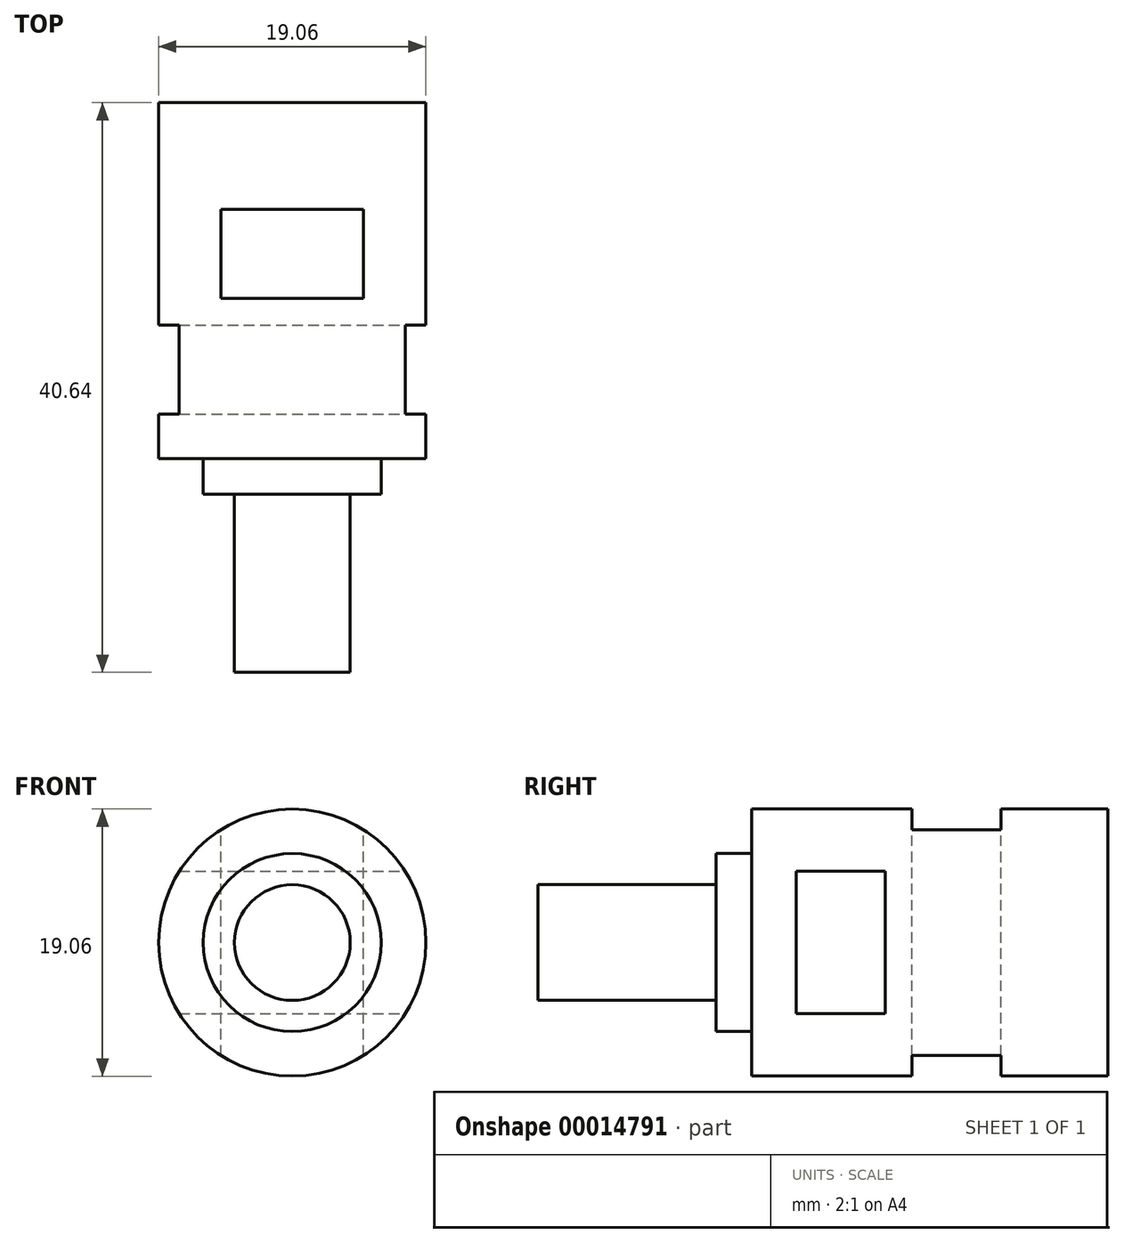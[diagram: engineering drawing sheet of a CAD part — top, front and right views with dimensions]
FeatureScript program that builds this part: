
annotation { "Feature Type Name" : "Feature", "Feature Type Description" : "" }
export const myFeature = defineFeature(function(context is Context, id is Id, definition is map)
    precondition{}
    {
        {
            var Q0;
            Q0=qCreatedBy(makeId("Front.planeOp"),FACE);
            var sketch = newSketch(context, id + "F0", { "sketchPlane" : qUnion([Q0])});
            skCircle(sketch, "E0", {"center": v(0, 0) * mm, "radius": 9.53 * mm});
            skSolve(sketch);
        }
        {
            var Q0;
            Q0=makeQuery(id+"F0.imprint","IMPRINT",FACE,{"disambiguationData":[TD([[makeQuery(id+"F0.imprint","IMPRINT",EDGE,{"derivedFrom":sQuery(id+"F0.wireOp",EDGE,"E0")}),1.0]])]});
            extrude(context, id + "F1", {"entities" : qUnion([Q0]), "depth" : 25.4 * mm});
        }
        {
            var Q0;
            Q0=makeQuery(id+"F1.opExtrude","CAP_FACE",FACE,{"disambiguationData":[OSD([sQuery(id+"F0.wireOp",EDGE,"E0")])],"isStart":false});
            var sketch = newSketch(context, id + "F2", { "sketchPlane" : qUnion([Q0])});
            skCircle(sketch, "E1", {"center": v(0, 0) * mm, "radius": 6.35 * mm});
            skSolve(sketch);
        }
        {
            var Q0;
            Q0=makeQuery(id+"F2.imprint","IMPRINT",FACE,{"disambiguationData":[TD([[makeQuery(id+"F2.imprint","IMPRINT",EDGE,{"derivedFrom":sQuery(id+"F2.wireOp",EDGE,"E1")}),1.0]])]});
            extrude(context, id + "F3", {"entities" : qUnion([Q0]), "operationType" : NewBodyOperationType.ADD, "depth" : 2.54 * mm});
        }
        {
            var Q0;
            Q0=makeQuery(id+"F3.opExtrude","CAP_FACE",FACE,{"disambiguationData":[OSD([sQuery(id+"F2.wireOp",EDGE,"E1")])],"isStart":false});
            var sketch = newSketch(context, id + "F4", { "sketchPlane" : qUnion([Q0])});
            skCircle(sketch, "E2", {"center": v(0, 0) * mm, "radius": 4.13 * mm});
            skSolve(sketch);
        }
        {
            var Q0;
            Q0=makeQuery(id+"F4.imprint","IMPRINT",FACE,{"disambiguationData":[TD([[makeQuery(id+"F4.imprint","IMPRINT",EDGE,{"derivedFrom":sQuery(id+"F4.wireOp",EDGE,"E2")}),1.0]])]});
            extrude(context, id + "F5", {"entities" : qUnion([Q0]), "operationType" : NewBodyOperationType.ADD, "depth" : 12.7 * mm});
        }
        {
            var Q0;
            Q0=qCreatedBy(makeId("Top.planeOp"),FACE);
            var sketch = newSketch(context, id + "F6", { "sketchPlane" : qUnion([Q0])});
            skLineSegment(sketch, "E3.rect.bottom", {"start": v(5.08, -13.97) * mm, "end": v(-5.08, -13.97) * mm});
            skLineSegment(sketch, "E3.rect.top", {"start": v(5.08, -7.62) * mm, "end": v(-5.08, -7.62) * mm});
            skLineSegment(sketch, "E3.rect.left", {"start": v(5.08, -13.97) * mm, "end": v(5.08, -7.62) * mm});
            skLineSegment(sketch, "E3.rect.right", {"start": v(-5.08, -13.97) * mm, "end": v(-5.08, -7.62) * mm});
            skPoint(sketch, "E3.rect.middle", {"position": v(0, -10.8) * mm});
            skSolve(sketch);
        }
        {
            var Q0;
            Q0=qCreatedBy(makeId("Right.planeOp"),FACE);
            var sketch = newSketch(context, id + "F7", { "sketchPlane" : qUnion([Q0])});
            skLineSegment(sketch, "E4.rect.bottom", {"start": v(-15.88, -5.08) * mm, "end": v(-22.23, -5.08) * mm});
            skLineSegment(sketch, "E4.rect.top", {"start": v(-15.88, 5.08) * mm, "end": v(-22.22, 5.08) * mm});
            skLineSegment(sketch, "E4.rect.left", {"start": v(-15.88, -5.08) * mm, "end": v(-15.87, 5.08) * mm});
            skLineSegment(sketch, "E4.rect.right", {"start": v(-22.23, -5.08) * mm, "end": v(-22.22, 5.08) * mm});
            skPoint(sketch, "E4.rect.middle", {"position": v(-19.05, 0) * mm});
            skSolve(sketch);
        }
        {
            var Q0;
            Q0=qSketchRegion(id+"F7",true);
            extrude(context, id + "F8", {"entities" : qUnion([Q0]), "operationType" : NewBodyOperationType.REMOVE, "oppositeDirection" : true, "depth" : 25.4 * mm, "hasSecondDirection" : true, "secondDirectionOppositeDirection" : false, "secondDirectionDepth" : 25.4 * mm});
        }
        {
            var Q0;
            Q0=qSketchRegion(id+"F6",true);
            extrude(context, id + "F9", {"entities" : qUnion([Q0]), "operationType" : NewBodyOperationType.REMOVE, "oppositeDirection" : true, "depth" : 12.7 * mm, "hasSecondDirection" : true, "secondDirectionOppositeDirection" : false, "secondDirectionDepth" : 12.7 * mm});
        }
    });
